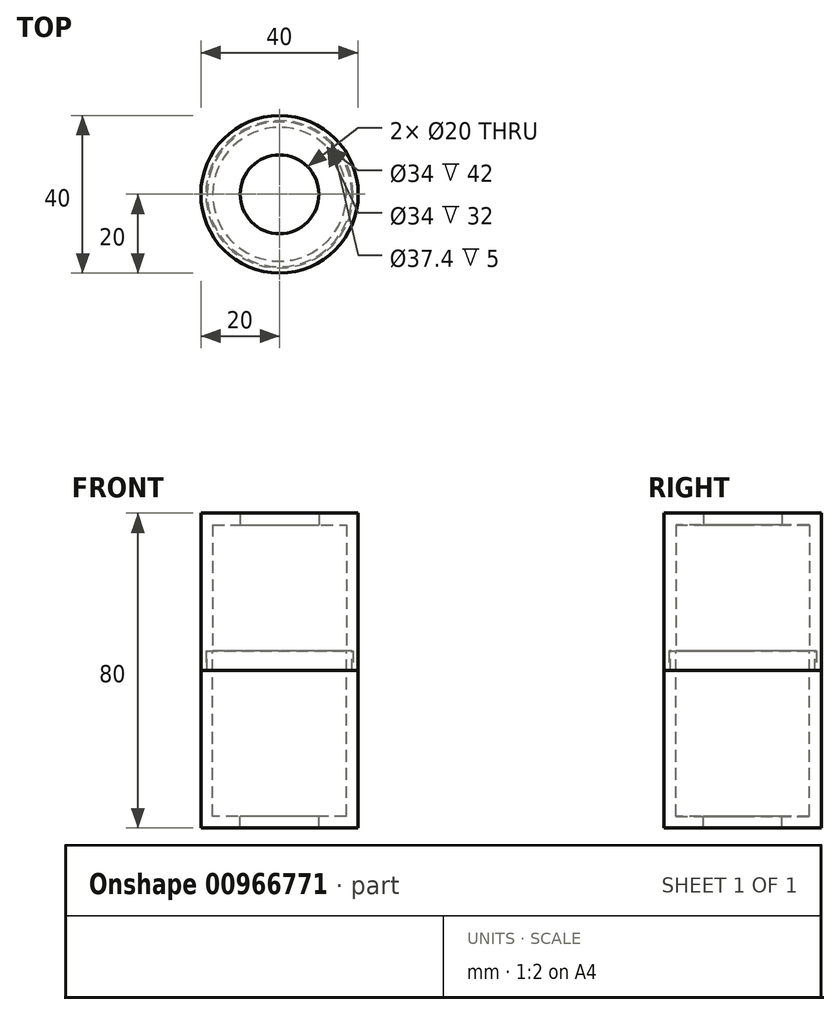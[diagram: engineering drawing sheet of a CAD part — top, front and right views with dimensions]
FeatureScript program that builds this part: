
annotation { "Feature Type Name" : "Feature", "Feature Type Description" : "" }
export const myFeature = defineFeature(function(context is Context, id is Id, definition is map)
    precondition{}
    {
        {
            var Q0;
            Q0=qCreatedBy(makeId("Front.planeOp"),FACE);
            var sketch = newSketch(context, id + "F0", { "sketchPlane" : qUnion([Q0])});
            skLineSegment(sketch, "E0", {"start": v(0, 0) * mm, "end": v(0, 40) * mm, "construction": true});
            skLineSegment(sketch, "E1", {"start": v(10, 40) * mm, "end": v(20, 40) * mm});
            skLineSegment(sketch, "E2", {"start": v(20, 40) * mm, "end": v(20, 0) * mm});
            skLineSegment(sketch, "E3.0", {"start": v(17, 37) * mm, "end": v(17, 5) * mm});
            skLineSegment(sketch, "E3.1", {"start": v(10, 37) * mm, "end": v(17, 37) * mm});
            skLineSegment(sketch, "E4", {"start": v(20, 0) * mm, "end": v(18.7, 0) * mm});
            skLineSegment(sketch, "E5", {"start": v(18.7, 0) * mm, "end": v(18.7, 5) * mm});
            skLineSegment(sketch, "E6", {"start": v(18.7, 5) * mm, "end": v(17, 5) * mm});
            skLineSegment(sketch, "E7", {"start": v(10, 37) * mm, "end": v(10, 40) * mm});
            skSolve(sketch);
        }
        {
            var Q0;
            Q0 = qSketchRegion(id + "F0", true);
            var Q1;
            Q1=sQuery(id+"F0.wireOp",EDGE,"E0");
            revolve(context, id + "F1", {"surfaceOperationType" : NewSurfaceOperationType.NEW, "entities" : qUnion([Q0]), "axis" : qUnion([Q1]), "revolveType" : RevolveType.FULL});
        }
        {
            var Q0;
            Q0=qCreatedBy(makeId("Front.planeOp"),FACE);
            var sketch = newSketch(context, id + "F2", { "sketchPlane" : qUnion([Q0])});
            skLineSegment(sketch, "E8", {"start": v(20, 0) * mm, "end": v(20, -40) * mm});
            skLineSegment(sketch, "E9", {"start": v(20, -40) * mm, "end": v(10, -40) * mm});
            skLineSegment(sketch, "E10.0", {"start": v(17, -37) * mm, "end": v(10, -37) * mm});
            skLineSegment(sketch, "E10.1", {"start": v(17, 0) * mm, "end": v(17, -37) * mm});
            skLineSegment(sketch, "E11", {"start": v(0, 0) * mm, "end": v(0, -19.9) * mm, "construction": true});
            skLineSegment(sketch, "E12", {"start": v(20, 0) * mm, "end": v(18.4, 0) * mm});
            skLineSegment(sketch, "E13", {"start": v(18.4, 0) * mm, "end": v(18.4, 5) * mm});
            skLineSegment(sketch, "E14", {"start": v(18.4, 5) * mm, "end": v(17, 5) * mm});
            skLineSegment(sketch, "E15", {"start": v(17, 5) * mm, "end": v(17, 0) * mm});
            skLineSegment(sketch, "E16", {"start": v(10, -40) * mm, "end": v(10, -37) * mm});
            skSolve(sketch);
        }
        {
            var Q0;
            Q0=makeQuery(id+"F2.imprint","IMPRINT",FACE,{"disambiguationData":[TD([[makeQuery(id+"F2.imprint","IMPRINT",EDGE,{"derivedFrom":sQuery(id+"F2.wireOp",EDGE,"E8")}),-1.0]])]});
            var Q1;
            Q1=sQuery(id+"F2.wireOp",EDGE,"E11");
            revolve(context, id + "F3", {"surfaceOperationType" : NewSurfaceOperationType.NEW, "entities" : qUnion([Q0]), "axis" : qUnion([Q1]), "revolveType" : RevolveType.FULL});
        }
    });
